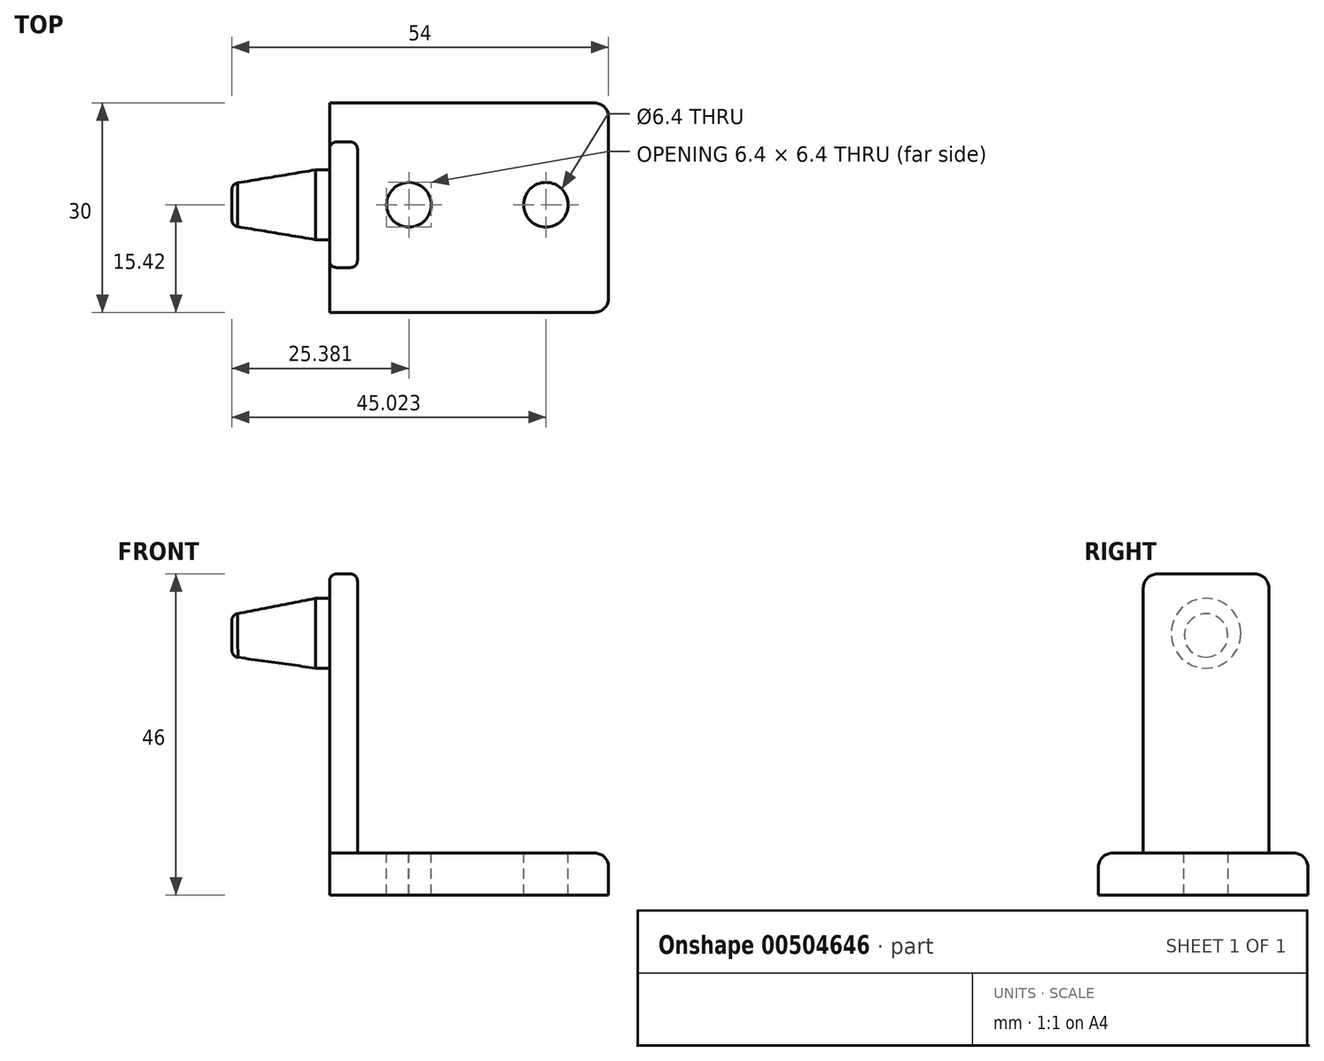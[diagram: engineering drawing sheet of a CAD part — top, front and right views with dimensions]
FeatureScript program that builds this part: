
annotation { "Feature Type Name" : "Feature", "Feature Type Description" : "" }
export const myFeature = defineFeature(function(context is Context, id is Id, definition is map)
    precondition{}
    {
        {
            var Q0;
            Q0=qCreatedBy(makeId("Top.planeOp"),FACE);
            var sketch = newSketch(context, id + "F0", { "sketchPlane" : qUnion([Q0])});
            skLineSegment(sketch, "E0.bottom", {"start": v(0, 14.58) * mm, "end": v(40, 14.58) * mm});
            skLineSegment(sketch, "E0.top", {"start": v(0, -15.42) * mm, "end": v(40, -15.42) * mm});
            skLineSegment(sketch, "E0.left", {"start": v(0, 14.58) * mm, "end": v(0, -15.42) * mm});
            skLineSegment(sketch, "E0.right", {"start": v(40, 14.58) * mm, "end": v(40, -15.42) * mm});
            skSolve(sketch);
        }
        {
            var Q0;
            Q0 = qSketchRegion(id + "F0", true);
            extrude(context, id + "F1", {"entities" : qUnion([Q0]), "depth" : 6 * mm});
        }
        {
            var Q0;
            Q0=makeQuery(id+"F1.opExtrude","CAP_FACE",FACE,{"disambiguationData":[OSD([sQuery(id+"F0.wireOp",EDGE,"E0.bottom"),sQuery(id+"F0.wireOp",EDGE,"E0.top"),sQuery(id+"F0.wireOp",EDGE,"E0.left"),sQuery(id+"F0.wireOp",EDGE,"E0.right")])],"isStart":false});
            var sketch = newSketch(context, id + "F2", { "sketchPlane" : qUnion([Q0])});
            skLineSegment(sketch, "E1.bottom", {"start": v(0, 9) * mm, "end": v(4, 9) * mm});
            skLineSegment(sketch, "E1.top", {"start": v(0, -9) * mm, "end": v(4, -9) * mm});
            skLineSegment(sketch, "E1.left", {"start": v(0, 9) * mm, "end": v(0, -9) * mm});
            skLineSegment(sketch, "E1.right", {"start": v(4, 9) * mm, "end": v(4, -9) * mm});
            skSolve(sketch);
        }
        {
            var Q0;
            Q0=makeQuery(id+"F2.imprint","IMPRINT",FACE,{"disambiguationData":[TD([[makeQuery(id+"F2.imprint","IMPRINT",EDGE,{"derivedFrom":sQuery(id+"F2.wireOp",EDGE,"E1.bottom")}),-1.0]])]});
            extrude(context, id + "F3", {"entities" : qUnion([Q0]), "operationType" : NewBodyOperationType.ADD, "depth" : 40 * mm});
        }
        {
            var Q0;
            Q0=makeQuery(id+"F3.opExtrude","SWEPT_FACE",FACE,{"disambiguationData":[OSD([sQuery(id+"F2.wireOp",EDGE,"E1.right")])]});
            var sketch = newSketch(context, id + "F4", { "sketchPlane" : qUnion([Q0])});
            skLineSegment(sketch, "E2", {"start": v(0, 46) * mm, "end": v(0, 6) * mm, "construction": true});
            skLineSegment(sketch, "E3", {"start": v(-9, 37.5) * mm, "end": v(9, 37.5) * mm});
            skCircle(sketch, "E4", {"center": v(0, 37.5) * mm, "radius": 5 * mm});
            skSolve(sketch);
        }
        {
            var Q0;
            Q0 = qSketchRegion(id + "F4", true);
            extrude(context, id + "F5", {"entities" : qUnion([Q0]), "operationType" : NewBodyOperationType.ADD, "oppositeDirection" : true, "depth" : 6 * mm});
        }
        {
            var Q0;
            Q0=makeQuery(id+"F5.opExtrude","CAP_FACE",FACE,{"disambiguationData":[OSD([sQuery(id+"F4.wireOp",EDGE,"E4")])],"isStart":false});
            cPlane(context, id + "F6", {"entities" : qUnion([Q0]), "cplaneType" : CPlaneType.OFFSET, "offset" : 12 * mm, "width" : 150 * mm, "height" : 150 * mm});
        }
        {
            var Q0;
            Q0=qCreatedBy(id+"F6.planeOp",FACE);
            var sketch = newSketch(context, id + "F7", { "sketchPlane" : qUnion([Q0])});
            skLineSegment(sketch, "E5", {"start": v(0, 37.17) * mm, "end": v(0, 37.17) * mm});
            skLineSegment(sketch, "E6", {"start": v(0, 37.17) * mm, "end": v(-8.55, 37.17) * mm, "construction": true});
            skCircle(sketch, "E7", {"center": v(0, 37.17) * mm, "radius": 3 * mm});
            skSolve(sketch);
        }
        {
            var Q0;
            Q0=makeQuery(id+"F5.opExtrude","CAP_FACE",FACE,{"disambiguationData":[OSD([sQuery(id+"F4.wireOp",EDGE,"E4")])],"isStart":false});
            var Q1;
            Q1=makeQuery(id+"F7.imprint","IMPRINT",FACE,{"disambiguationData":[TD([[makeQuery(id+"F7.imprint","IMPRINT",EDGE,{"derivedFrom":sQuery(id+"F7.wireOp",EDGE,"E7")}),1.0]])]});
            loft(context, id + "F8", {"sheetProfilesArray" : [{ "sheetProfileEntities" : qUnion([Q0]) }, { "sheetProfileEntities" : qUnion([Q1]) }]});
        }
        {
            var Q0;
            Q0=makeQuery(id+"F1.opExtrude","CAP_FACE",FACE,{"disambiguationData":[OSD([sQuery(id+"F0.wireOp",EDGE,"E0.bottom"),sQuery(id+"F0.wireOp",EDGE,"E0.top"),sQuery(id+"F0.wireOp",EDGE,"E0.left"),sQuery(id+"F0.wireOp",EDGE,"E0.right")])],"isStart":false});
            var sketch = newSketch(context, id + "F9", { "sketchPlane" : qUnion([Q0])});
            skCircle(sketch, "E8", {"center": v(11.38, 0) * mm, "radius": 3.2 * mm});
            skCircle(sketch, "E9", {"center": v(31.02, 0) * mm, "radius": 3.2 * mm});
            skLineSegment(sketch, "E10", {"start": v(11.34, 3.2) * mm, "end": v(31.02, 3.2) * mm});
            skLineSegment(sketch, "E11", {"start": v(11.67, -3.19) * mm, "end": v(31.02, -3.2) * mm});
            skSolve(sketch);
        }
        {
            var Q0;
            {var subQ0=sQuery(id+"F9.wireOp",EDGE,"E9");var subQ1=makeQuery(id+"F9.imprint","INTERSECT",VERTEX,{"derivedFrom":[subQ0,sQuery(id+"F9.wireOp",EDGE,"E10")]});Q0=makeQuery(id+"F9.imprint","IMPRINT",FACE,{"disambiguationData":[TD([[makeQuery(id+"F9.imprint","IMPRINT",EDGE,{"disambiguationData":[TD([[subQ1,-1.0]])],"derivedFrom":subQ0}),1.0]])]});}
            var Q1;
            {var subQ0=sQuery(id+"F9.wireOp",EDGE,"E10");Q1=makeQuery(id+"F9.imprint","IMPRINT",FACE,{"disambiguationData":[TD([[makeQuery(id+"F9.imprint","IMPRINT",EDGE,{"derivedFrom":subQ0}),-1.0]])]});}
            var Q2;
            {var subQ0=sQuery(id+"F9.wireOp",EDGE,"E8");var subQ2=makeQuery(id+"F9.imprint","IMPRINT",VERTEX,{"derivedFrom":subQ0});Q2=makeQuery(id+"F9.imprint","IMPRINT",FACE,{"disambiguationData":[TD([[makeQuery(id+"F9.imprint","IMPRINT",EDGE,{"disambiguationData":[TD([[subQ2,1.0]])],"derivedFrom":subQ0}),1.0]])]});}
            extrude(context, id + "F10", {"entities" : qUnion([Q0, Q1, Q2]), "operationType" : NewBodyOperationType.REMOVE, "endBound" : BoundingType.THROUGH_ALL, "oppositeDirection" : true, "depth" : 25 * mm});
        }
        {
            var Q0;
            Q0=makeQuery(id+"F3.opExtrude","CAP_EDGE",EDGE,{"disambiguationData":[OSD([sQuery(id+"F2.wireOp",EDGE,"E1.right")])],"isStart":false});
            var Q1;
            Q1=makeQuery(id+"F3.opExtrude","SWEPT_EDGE",EDGE,{"disambiguationData":[OSD([sQuery(id+"F2.wireOp",EDGE,"E1.top"),sQuery(id+"F2.wireOp",EDGE,"E1.right")])]});
            var Q2;
            Q2=makeQuery(id+"F3.opExtrude","SWEPT_EDGE",EDGE,{"disambiguationData":[OSD([sQuery(id+"F2.wireOp",EDGE,"E1.bottom"),sQuery(id+"F2.wireOp",EDGE,"E1.right")])]});
            var Q3;
            Q3=makeQuery(id+"F3.opExtrude","CAP_EDGE",EDGE,{"disambiguationData":[OSD([sQuery(id+"F2.wireOp",EDGE,"E1.right")])],"isStart":true});
            var Q4;
            {var subQ0=sQuery(id+"F2.wireOp",EDGE,"E1.top");var subQ1=sQuery(id+"F0.wireOp",EDGE,"E0.left");var subQ2=sQuery(id+"F2.wireOp",EDGE,"E1.left");Q4=makeQuery(id+"F5.boolean.opBoolean","SPLIT",EDGE,{"disambiguationData":[TD([makeQuery(id+"F1.opExtrude","CAP_FACE",FACE,{"disambiguationData":[OSD([sQuery(id+"F0.wireOp",EDGE,"E0.bottom"),sQuery(id+"F0.wireOp",EDGE,"E0.top"),subQ1,sQuery(id+"F0.wireOp",EDGE,"E0.right")])],"isStart":false})])],"derivedFrom":makeQuery(id+"F3.opExtrude","SWEPT_EDGE",EDGE,{"disambiguationData":[OSD([subQ1,subQ0,subQ2])]})});}
            var Q5;
            {var subQ0=sQuery(id+"F2.wireOp",EDGE,"E1.bottom");var subQ1=sQuery(id+"F0.wireOp",EDGE,"E0.left");var subQ2=sQuery(id+"F2.wireOp",EDGE,"E1.left");Q5=makeQuery(id+"F5.boolean.opBoolean","SPLIT",EDGE,{"disambiguationData":[TD([makeQuery(id+"F1.opExtrude","CAP_FACE",FACE,{"disambiguationData":[OSD([sQuery(id+"F0.wireOp",EDGE,"E0.bottom"),sQuery(id+"F0.wireOp",EDGE,"E0.top"),subQ1,sQuery(id+"F0.wireOp",EDGE,"E0.right")])],"isStart":false})])],"derivedFrom":makeQuery(id+"F3.opExtrude","SWEPT_EDGE",EDGE,{"disambiguationData":[OSD([subQ1,subQ0,subQ2])]})});}
            var Q6;
            Q6=makeQuery(id+"F3.opExtrude","CAP_EDGE",EDGE,{"disambiguationData":[OSD([sQuery(id+"F2.wireOp",EDGE,"E1.left")])],"isStart":false});
            var Q7;
            Q7=makeQuery(id+"F8.opLoft","MID_CAP_EDGE",EDGE,{"disambiguationData":[OSD([sQuery(id+"F4.wireOp",EDGE,"E4"),sQuery(id+"F7.wireOp",EDGE,"E7")])],"capPos":1.0});
            fillet(context, id + "F11", {"entities" : qUnion([Q0, Q1, Q2, Q3, Q4, Q5, Q6, Q7]), "radius" : 1 * mm, "tangentPropagation" : true, "allowEdgeOverflow" : false});
        }
        {
            var Q0;
            Q0=makeQuery(id+"F3.opExtrude","CAP_EDGE",EDGE,{"disambiguationData":[OSD([sQuery(id+"F2.wireOp",EDGE,"E1.bottom")])],"isStart":false});
            var Q1;
            Q1=makeQuery(id+"F3.opExtrude","CAP_EDGE",EDGE,{"disambiguationData":[OSD([sQuery(id+"F2.wireOp",EDGE,"E1.top")])],"isStart":false});
            var Q2;
            Q2=makeQuery(id+"F1.opExtrude","CAP_EDGE",EDGE,{"disambiguationData":[OSD([sQuery(id+"F0.wireOp",EDGE,"E0.top")])],"isStart":false});
            var Q3;
            Q3=makeQuery(id+"F1.opExtrude","CAP_EDGE",EDGE,{"disambiguationData":[OSD([sQuery(id+"F0.wireOp",EDGE,"E0.right")])],"isStart":false});
            var Q4;
            Q4=makeQuery(id+"F1.opExtrude","CAP_EDGE",EDGE,{"disambiguationData":[OSD([sQuery(id+"F0.wireOp",EDGE,"E0.bottom")])],"isStart":false});
            var Q5;
            Q5=makeQuery(id+"F1.opExtrude","SWEPT_EDGE",EDGE,{"disambiguationData":[OSD([sQuery(id+"F0.wireOp",EDGE,"E0.top"),sQuery(id+"F0.wireOp",EDGE,"E0.right")])]});
            var Q6;
            Q6=makeQuery(id+"F1.opExtrude","SWEPT_EDGE",EDGE,{"disambiguationData":[OSD([sQuery(id+"F0.wireOp",EDGE,"E0.bottom"),sQuery(id+"F0.wireOp",EDGE,"E0.right")])]});
            fillet(context, id + "F12", {"entities" : qUnion([Q0, Q1, Q2, Q3, Q4, Q5, Q6]), "radius" : 2 * mm, "tangentPropagation" : true, "allowEdgeOverflow" : false});
        }
    });
